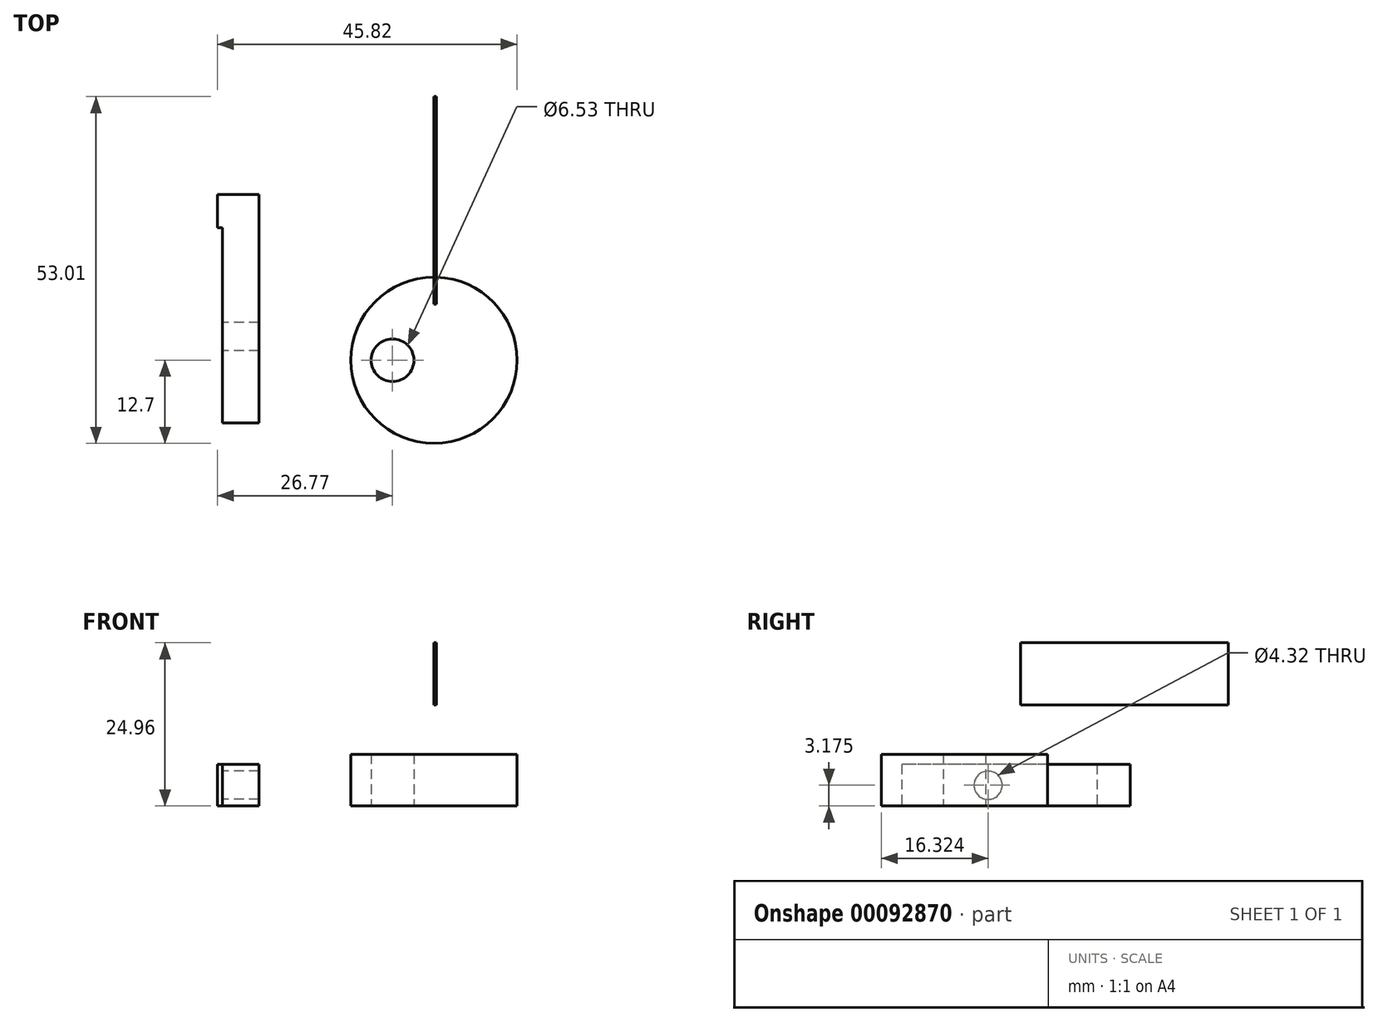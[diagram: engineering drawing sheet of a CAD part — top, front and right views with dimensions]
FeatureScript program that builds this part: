
annotation { "Feature Type Name" : "Feature", "Feature Type Description" : "" }
export const myFeature = defineFeature(function(context is Context, id is Id, definition is map)
    precondition{}
    {
        {
            var Q0;
            Q0=qCreatedBy(makeId("Top.planeOp"),FACE);
            var sketch = newSketch(context, id + "F0", { "sketchPlane" : qUnion([Q0])});
            skCircle(sketch, "E0", {"center": v(0, 0) * mm, "radius": 12.7 * mm});
            skLineSegment(sketch, "E1", {"start": v(-12.7, 0) * mm, "end": v(12.7, 0) * mm, "construction": true});
            skLineSegment(sketch, "E2", {"start": v(-6.35, 11) * mm, "end": v(-6.35, -11) * mm, "construction": true});
            skPoint(sketch, "E3", {"position": v(-6.35, 0) * mm});
            skSolve(sketch);
        }
        {
            var Q0;
            Q0=makeQuery(id+"F0.imprint","IMPRINT",FACE,{"disambiguationData":[TD([[makeQuery(id+"F0.imprint","IMPRINT",EDGE,{"derivedFrom":sQuery(id+"F0.wireOp",EDGE,"E0")}),1.0]])]});
            extrude(context, id + "F1", {"entities" : qUnion([Q0]), "depth" : 7.92 * mm});
        }
        {
            var Q0;
            Q0=sQuery(id+"F0.wireOp",VERTEX,"E3");
            var Q1;
            Q1=makeQuery(id+"F1.opExtrude","SWEPT_BODY",BODY,{"disambiguationData":[OSD([sQuery(id+"F0.wireOp",EDGE,"E0")])]});
            hole(context, id + "F2", {"style" : HoleStyle.SIMPLE, "endStyle" : HoleEndStyle.THROUGH, "oppositeDirection" : true, "standardTappedOrClearance" : lookupTablePath({ "standard" : "ANSI", "fit" : "Close", "size" : "1/4", "type" : "Clearance" }), "standardBlindInLast" : lookupTablePath({ "fit" : "Close", "standard" : "ANSI", "size" : "1/4", "type" : "Clearance" }), "holeDiameter" : 6.53 * mm, "locations" : qUnion([Q0]), "scope" : qUnion([Q1]), "isTappedThrough" : true});
        }
        {
            var Q0;
            Q0=qCreatedBy(makeId("Top.planeOp"),FACE);
            var sketch = newSketch(context, id + "F3", { "sketchPlane" : qUnion([Q0])});
            skLineSegment(sketch, "E4.bottom", {"start": v(-33.12, 25.34) * mm, "end": v(-26.77, 25.34) * mm});
            skLineSegment(sketch, "E4.top", {"start": v(-32.33, -9.59) * mm, "end": v(-26.77, -9.59) * mm});
            skLineSegment(sketch, "E4.left", {"start": v(-33.12, 25.34) * mm, "end": v(-33.12, 20.26) * mm});
            skLineSegment(sketch, "E4.right", {"start": v(-26.77, 25.34) * mm, "end": v(-26.77, -9.59) * mm});
            skLineSegment(sketch, "E5", {"start": v(-32.33, 20.26) * mm, "end": v(-26.77, 20.26) * mm, "construction": true});
            skLineSegment(sketch, "E6", {"start": v(-32.33, 20.26) * mm, "end": v(-32.33, -9.59) * mm});
            skLineSegment(sketch, "E7", {"start": v(-33.12, 20.26) * mm, "end": v(-32.33, 20.26) * mm});
            skSolve(sketch);
        }
        {
            var Q0;
            Q0=makeQuery(id+"F3.imprint","IMPRINT",FACE,{"disambiguationData":[TD([[makeQuery(id+"F3.imprint","IMPRINT",EDGE,{"derivedFrom":sQuery(id+"F3.wireOp",EDGE,"E4.bottom")}),-1.0]])]});
            extrude(context, id + "F4", {"entities" : qUnion([Q0]), "depth" : 6.35 * mm});
        }
        {
            var Q0;
            Q0=makeQuery(id+"F4.opExtrude","SWEPT_FACE",FACE,{"disambiguationData":[OSD([sQuery(id+"F3.wireOp",EDGE,"E6")])]});
            var sketch = newSketch(context, id + "F5", { "sketchPlane" : qUnion([Q0])});
            skLineSegment(sketch, "E8", {"start": v(-3.62, 6.35) * mm, "end": v(-3.62, 0) * mm, "construction": true});
            skPoint(sketch, "E9", {"position": v(-3.62, 3.18) * mm});
            skSolve(sketch);
        }
        {
            var Q0;
            Q0=sQuery(id+"F5.wireOp",VERTEX,"E9");
            var Q1;
            Q1=makeQuery(id+"F4.opExtrude","SWEPT_BODY",BODY,{"disambiguationData":[OSD([sQuery(id+"F3.wireOp",EDGE,"E4.bottom"),sQuery(id+"F3.wireOp",EDGE,"E4.top"),sQuery(id+"F3.wireOp",EDGE,"E4.left"),sQuery(id+"F3.wireOp",EDGE,"E4.right"),sQuery(id+"F3.wireOp",EDGE,"E6"),sQuery(id+"F3.wireOp",EDGE,"E7")])]});
            hole(context, id + "F6", {"style" : HoleStyle.SIMPLE, "endStyle" : HoleEndStyle.THROUGH, "standardTappedOrClearance" : lookupTablePath({ "standard" : "ANSI", "fit" : "Close", "size" : "#8", "type" : "Clearance" }), "standardBlindInLast" : lookupTablePath({ "fit" : "Close", "standard" : "ANSI", "size" : "#8", "type" : "Clearance" }), "holeDiameter" : 4.32 * mm, "locations" : qUnion([Q0]), "scope" : qUnion([Q1]), "isTappedThrough" : true});
        }
        {
            var Q0;
            Q0=qCreatedBy(makeId("Right.planeOp"),FACE);
            var sketch = newSketch(context, id + "F7", { "sketchPlane" : qUnion([Q0])});
            skLineSegment(sketch, "E10.bottom", {"start": v(40.31, 24.96) * mm, "end": v(8.56, 24.96) * mm});
            skLineSegment(sketch, "E10.top", {"start": v(40.31, 15.44) * mm, "end": v(8.56, 15.44) * mm});
            skLineSegment(sketch, "E10.left", {"start": v(40.31, 24.96) * mm, "end": v(40.31, 15.44) * mm});
            skLineSegment(sketch, "E10.right", {"start": v(8.56, 24.96) * mm, "end": v(8.56, 15.44) * mm});
            skSolve(sketch);
        }
        {
            var Q0;
            Q0=makeQuery(id+"F7.imprint","IMPRINT",FACE,{"disambiguationData":[TD([[makeQuery(id+"F7.imprint","IMPRINT",EDGE,{"derivedFrom":sQuery(id+"F7.wireOp",EDGE,"E10.bottom")}),1.0]])]});
            extrude(context, id + "F8", {"entities" : qUnion([Q0]), "depth" : 0.38 * mm});
        }
    });
